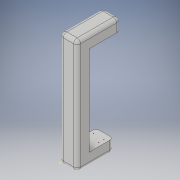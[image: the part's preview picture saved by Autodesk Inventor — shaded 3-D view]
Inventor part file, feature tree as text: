
AUTODESK INVENTOR PART (.ipt)
format: ipt  version: 2018 (Build 220112000, 112)  size: 200,704 bytes
history: native  units: in
note: dims shown in document units (in); Inventor stores cm internally (conversion verified against a paired STEP export)
features: sketch x6, extrude x5, fillet x1
ambient origin geometry x8: Origin, YZ Plane, XZ Plane, XY Plane, X Axis, Y Axis, Z Axis, Center Point
bodies: Solid1 (feature_tree)
feature tree (12):
  sketch  "Sketch1"  dims[d0=26.0in d1=7.0in d2=9.0in]
  extrude  "Extrusion1"  Depth=7.0in
  fillet  "Fillet1"  Radius=9.0in
  extrude  "Extrusion2"  Depth=3.5in
  extrude  "Extrusion3"  Depth=5.0in TaperAngle=0.0deg
  extrude  "Extrusion5"  Depth=1.0in
  extrude  "Extrusion6"  Depth=0.125in TaperAngle=0.0deg
  sketch  "Sketch2"  dims[d3=3.5in d4=3.5in]
  sketch  "Sketch3"  dims[d5=3.5in d6=5.0in d7=0.0in]
  sketch  "Sketch4"  dims[d8=1.0in d9=10.0in]
  sketch  "Sketch5"  dims[d10=6.0in d14=0.125in d15=0.0in]
  sketch  "Sketch6"  dims[d23=1.5in d24=1.5in d25=1.5in d26=11.5in d27=3.0in d28=1.5in d30=1.5in d31=0.2in d32=0.125in d33=0.0in d34=3.438in d35=3.003in d36=3.438in d37=0.2in d40=2.0in d41=0.125in d42=0.0in d43=1.0in d44=1.0in d45=0.75in d46=1.5in d47=0.2in d48=0.125in d49=0.0in d50=1.5in d51=1.5in]
